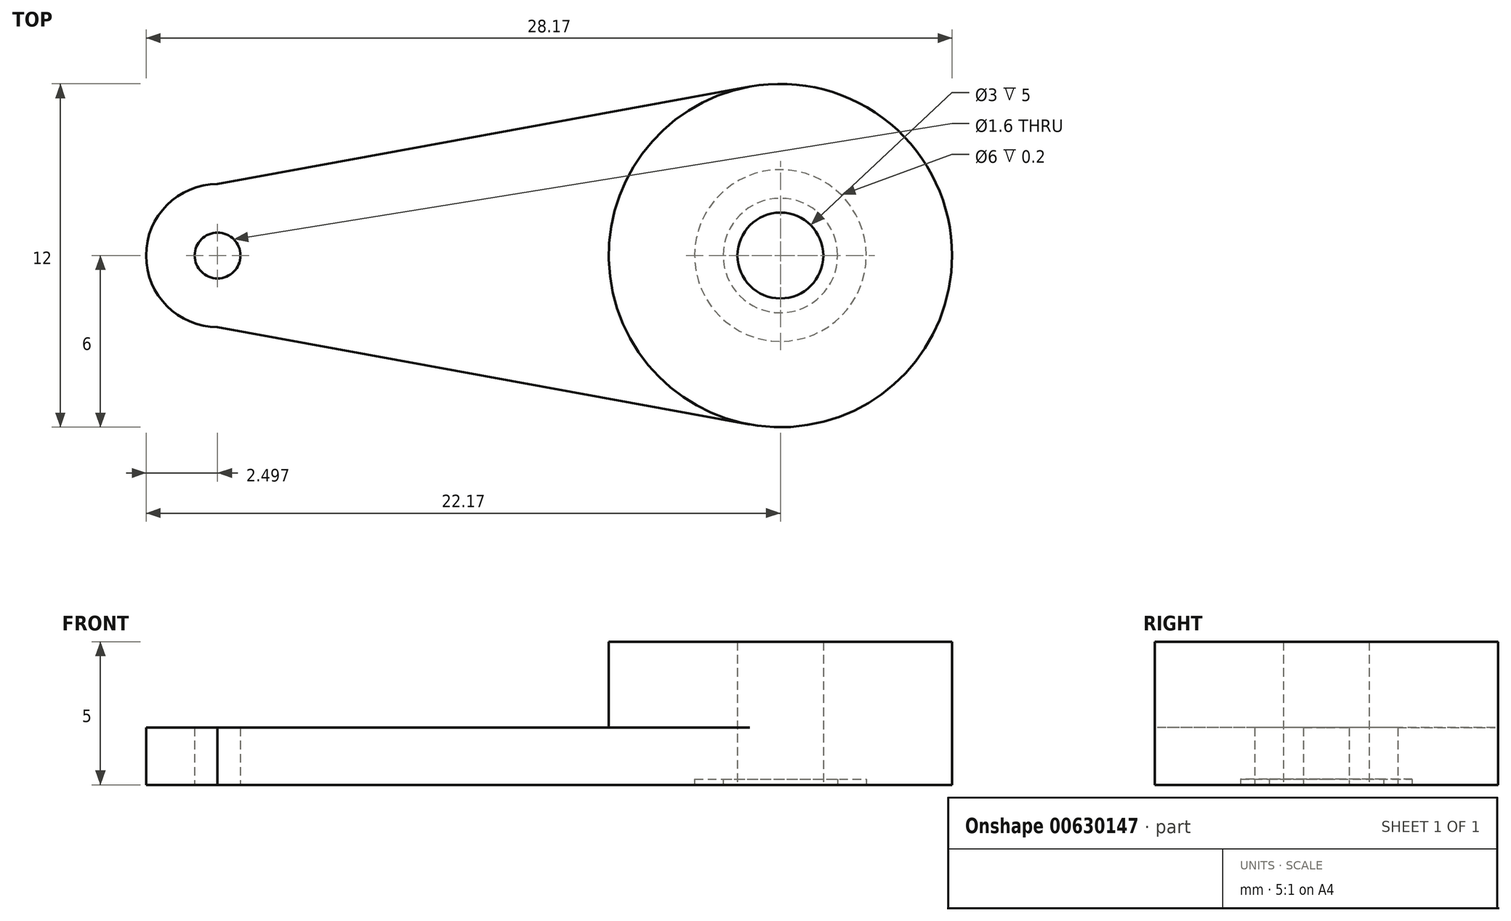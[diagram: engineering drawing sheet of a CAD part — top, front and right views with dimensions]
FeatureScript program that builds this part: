
annotation { "Feature Type Name" : "Feature", "Feature Type Description" : "" }
export const myFeature = defineFeature(function(context is Context, id is Id, definition is map)
    precondition{}
    {
        {
            var Q0;
            Q0=qCreatedBy(makeId("Top.planeOp"),FACE);
            var sketch = newSketch(context, id + "F0", { "sketchPlane" : qUnion([Q0])});
            skCircle(sketch, "E0", {"center": v(0, 0) * mm, "radius": 6 * mm});
            skCircle(sketch, "E1", {"center": v(-19.67, 0) * mm, "radius": 2.5 * mm});
            skLineSegment(sketch, "E2", {"start": v(-19.67, 2.5) * mm, "end": v(0, 6.1) * mm});
            skLineSegment(sketch, "E3", {"start": v(-19.67, -2.5) * mm, "end": v(0, -6.1) * mm});
            skCircle(sketch, "E4", {"center": v(0, 0) * mm, "radius": 1.5 * mm});
            skCircle(sketch, "E5", {"center": v(-19.67, 0) * mm, "radius": 0.8 * mm});
            skSolve(sketch);
        }
        {
            var Q0;
            Q0=makeQuery(id+"F0.imprint","IMPRINT",FACE,{"disambiguationData":[TD([[makeQuery(id+"F0.imprint","IMPRINT",EDGE,{"derivedFrom":sQuery(id+"F0.wireOp",EDGE,"E4")}),-1.0]])]});
            extrude(context, id + "F1", {"entities" : qUnion([Q0]), "depth" : 5 * mm});
        }
        {
            var Q0;
            {var subQ0=sQuery(id+"F0.wireOp",EDGE,"E2");var subQ1=sQuery(id+"F0.wireOp",EDGE,"E0");var subQ2=makeQuery(id+"F0.imprint","INTERSECT",VERTEX,{"derivedFrom":[subQ1,subQ0]});Q0=makeQuery(id+"F0.imprint","IMPRINT",FACE,{"disambiguationData":[TD([[makeQuery(id+"F0.imprint","IMPRINT",EDGE,{"disambiguationData":[TD([[subQ2,-1.0]])],"derivedFrom":subQ1}),-1.0]])]});}
            var Q1;
            Q1=makeQuery(id+"F0.imprint","IMPRINT",FACE,{"disambiguationData":[TD([[makeQuery(id+"F0.imprint","IMPRINT",EDGE,{"derivedFrom":sQuery(id+"F0.wireOp",EDGE,"E5")}),-1.0]])]});
            extrude(context, id + "F2", {"entities" : qUnion([Q0, Q1]), "operationType" : NewBodyOperationType.ADD, "depth" : 2 * mm});
        }
        {
            var Q0;
            {var subQ0=sQuery(id+"F0.wireOp",EDGE,"E0");Q0=makeQuery(id+"F2.boolean.opBoolean","MERGE",FACE,{"derivedFrom":[makeQuery(id+"F1.opExtrude","CAP_FACE",FACE,{"disambiguationData":[OSD([subQ0,sQuery(id+"F0.wireOp",EDGE,"E4")])],"isStart":true}),makeQuery(id+"F2.opExtrude","CAP_FACE",FACE,{"disambiguationData":[OSD([subQ0,sQuery(id+"F0.wireOp",EDGE,"E1"),sQuery(id+"F0.wireOp",EDGE,"E2"),sQuery(id+"F0.wireOp",EDGE,"E3"),sQuery(id+"F0.wireOp",EDGE,"E5")])],"isStart":true})]});}
            var sketch = newSketch(context, id + "F3", { "sketchPlane" : qUnion([Q0])});
            skCircle(sketch, "E6", {"center": v(0, 0) * mm, "radius": 2 * mm});
            skCircle(sketch, "E7", {"center": v(0, 0) * mm, "radius": 3 * mm});
            skSolve(sketch);
        }
        {
            var Q0;
            Q0=qSketchRegion(id+"F3",true);
            extrude(context, id + "F4", {"entities" : qUnion([Q0]), "operationType" : NewBodyOperationType.REMOVE, "oppositeDirection" : true, "depth" : 0.2 * mm});
        }
    });
